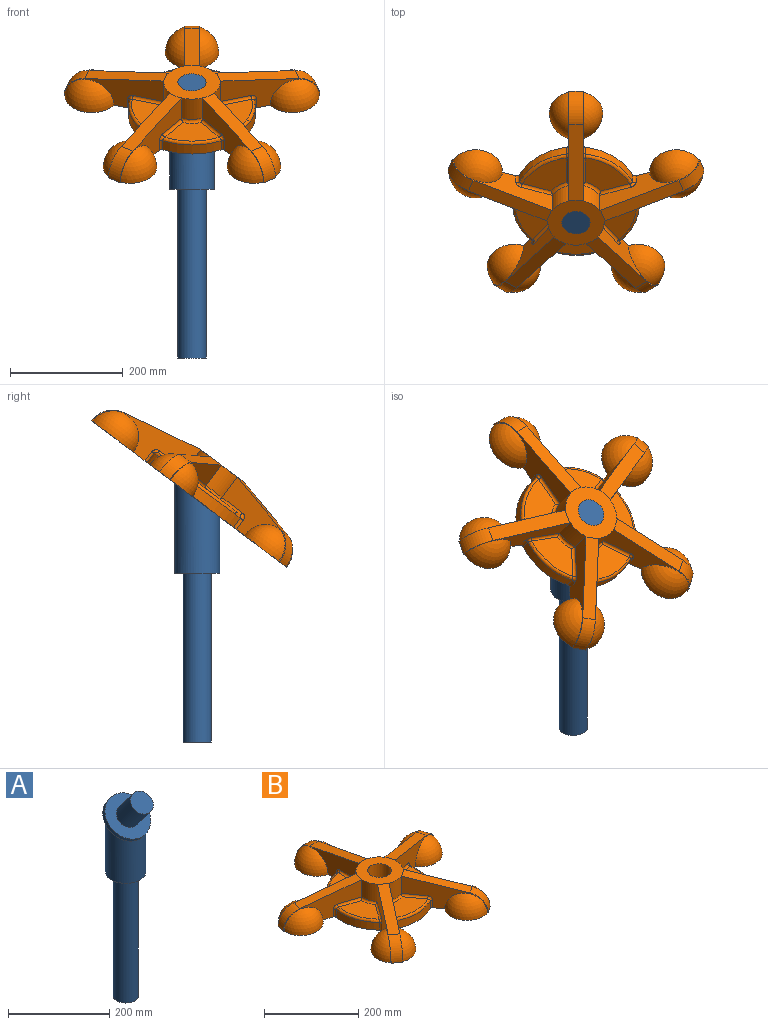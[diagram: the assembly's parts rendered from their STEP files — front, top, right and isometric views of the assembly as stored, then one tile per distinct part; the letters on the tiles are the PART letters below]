
ASSEMBLY  parts=2 mates=1
PART A: 10 faces, bbox 100x105x505 mm
  f0: cylinder r=25mm len=300mm, axis (0,0,1), area 47123.9mm2, adj f1,f3
  f1: plane 50x50mm, normal (0,0,-1), area 1963.5mm2, adj f0
  f2: cylinder r=40mm len=160mm, axis (0,0,-1), area 32672.6mm2, adj f3,f4,f7
  f3: plane 80x80mm, normal (0,0,-1), area 3063.1mm2, adj f0,f2
  f4: plane 80x60mm, normal (0,0.6,-0.8), area 785.4mm2, adj f2,f5
  f5: cylinder r=50mm len=100mm, axis (0,0.6,-0.8), area 3141.6mm2, adj f4,f6,f7
  f6: plane 100x80mm, normal (0,-0.6,0.8), area 5890.5mm2, adj f5,f8
  f7: plane 80x60mm, normal (0,0.6,-0.8), area 785.4mm2, adj f2,f5
  f8: cylinder r=25mm len=82mm, axis (0,0.6,-0.8), area 10210.2mm2, adj f6,f9
  f9: plane 50x40mm, normal (0,-0.6,0.8), area 1963.5mm2, adj f8
PART B: 95 faces, bbox 454.7x434.2x75 mm
  f0: plane 186.59x75mm, normal (1,0,0), area 5066mm2, adj f14,f17,f18,f19,f20,f22,f90,f91
  f1: plane 186.59x75mm, normal (-1,0,0), area 5066mm2, adj f13,f14,f15,f18,f19,f20,f65,f67
  f2: plane 150.95x109.67mm, normal (-0.81,-0.59,0), area 5066mm2, adj f11,f14,f20,f24,f25,f27,f58,f59
  f3: plane 150.95x109.67mm, normal (0.81,0.59,0), area 5066mm2, adj f10,f14,f20,f25,f26,f27,f81,f83
  f4: plane 150.95x109.67mm, normal (-0.81,0.59,0), area 5066mm2, adj f12,f14,f20,f28,f29,f32,f74,f75
  f5: plane 150.95x109.67mm, normal (0.81,-0.59,0), area 5066mm2, adj f11,f14,f20,f29,f30,f32,f53,f54
  f6: plane 177.46x75mm, normal (0.31,0.95,0), area 5066mm2, adj f13,f14,f20,f33,f34,f37,f61,f62
  f7: plane 177.46x75mm, normal (-0.31,-0.95,0), area 5066mm2, adj f12,f14,f20,f34,f35,f37,f69,f70
  f8: plane 177.46x75mm, normal (0.31,-0.95,0), area 5066mm2, adj f10,f14,f20,f40,f41,f42,f77,f78
  f9: plane 177.46x75mm, normal (-0.31,0.95,0), area 5066mm2, adj f14,f20,f22,f38,f41,f42,f85,f86
  f10: cylinder r=50mm len=45mm, axis (0,0,-1), area 1690.4mm2, adj f3,f8,f20,f79
  f11: cylinder r=50mm len=45mm, axis (0,0,-1), area 1690.4mm2, adj f2,f5,f20,f56
  f12: cylinder r=50mm len=45mm, axis (0,0,-1), area 1690.4mm2, adj f4,f7,f20,f72
  f13: cylinder r=50mm len=45mm, axis (0,0,-1), area 1690.4mm2, adj f1,f6,f20,f63
  f14: plane 454.72x434.19mm, normal (0,0,-1), area 48902.3mm2, adj f0,f1,f2,f3,f4,f5,f6,f7
  f15: sphere r=47.5mm, area 5222.9mm2, adj f1,f14
  f16: sphere r=37.5mm, area 8835.7mm2, adj f14
  f17: sphere r=47.5mm, area 5222.9mm2, adj f0,f14
  f18: cylinder r=47.5mm len=46.63mm, axis (-1,0,0), area 1638.2mm2, adj f0,f1,f14,f19
  f19: plane 146.53x28.37mm, normal (0,0.19,0.98), area 3731.2mm2, adj f0,f1,f18,f20
  f20: plane 102.83x100mm, normal (0,0,1), area 5956.2mm2, adj f0,f1,f2,f3,f4,f5,f6,f7
  f21: cylinder r=25mm len=65mm, axis (0,0,-1), area 10210.2mm2, adj f20,f94
  f22: cylinder r=50mm len=45mm, axis (0,0,-1), area 1690.4mm2, adj f0,f9,f20,f88
  f23: sphere r=37.5mm, area 8835.7mm2, adj f14
  f24: sphere r=47.5mm, area 5222.9mm2, adj f2,f14
  f25: cylinder r=47.5mm len=46.63mm, axis (0.81,0.59,0), area 1638.2mm2, adj f2,f3,f14,f27
  f26: sphere r=47.5mm, area 5222.9mm2, adj f3,f14
  f27: plane 133.24x106.35mm, normal (0.11,-0.15,0.98), area 3731.2mm2, adj f2,f3,f20,f25
  f28: sphere r=47.5mm, area 5222.9mm2, adj f4,f14
  f29: cylinder r=47.5mm len=46.63mm, axis (0.81,-0.59,0), area 1638.2mm2, adj f4,f5,f14,f32
  f30: sphere r=47.5mm, area 5222.9mm2, adj f5,f14
  f31: sphere r=37.5mm, area 8835.7mm2, adj f14
  f32: plane 133.24x106.35mm, normal (-0.11,-0.15,0.98), area 3731.2mm2, adj f4,f5,f20,f29
  f33: sphere r=47.5mm, area 5222.9mm2, adj f6,f14
  f34: cylinder r=47.5mm len=46.63mm, axis (-0.31,-0.95,0), area 1638.2mm2, adj f6,f7,f14,f37
  f35: sphere r=47.5mm, area 5222.9mm2, adj f7,f14
  f36: sphere r=37.5mm, area 8835.7mm2, adj f14
  f37: plane 147.08x69.06mm, normal (-0.18,0.06,0.98), area 3731.2mm2, adj f6,f7,f20,f34
  f38: sphere r=47.5mm, area 5222.9mm2, adj f9,f14
  f39: sphere r=37.5mm, area 8835.7mm2, adj f14
  f40: sphere r=47.5mm, area 5222.9mm2, adj f8,f14
  f41: cylinder r=47.5mm len=46.63mm, axis (-0.31,0.95,0), area 1638.2mm2, adj f8,f9,f14,f42
  f42: plane 147.08x69.06mm, normal (0.18,0.06,0.98), area 3731.2mm2, adj f8,f9,f20,f41
  f43: plane 77.97x73.31mm, normal (0,0,1), area 3506.5mm2, adj f86,f88,f89,f90
  f44: cylinder r=112.5mm len=83.87mm, axis (0,0,-1), area 2154.7mm2, adj f14,f85,f89,f92
  f45: plane 91.66x62.69mm, normal (0,0,1), area 3506.5mm2, adj f77,f79,f81,f82
  f46: cylinder r=112.5mm len=98.59mm, axis (0,0,-1), area 2154.7mm2, adj f14,f78,f82,f84
  f47: plane 91.66x62.69mm, normal (0,0,1), area 3506.5mm2, adj f70,f72,f73,f74
  f48: cylinder r=112.5mm len=98.59mm, axis (0,0,-1), area 2154.7mm2, adj f14,f69,f73,f76
  f49: plane 77.97x73.31mm, normal (0,0,1), area 3506.5mm2, adj f61,f63,f65,f66
  f50: cylinder r=112.5mm len=83.87mm, axis (0,0,-1), area 2154.7mm2, adj f14,f62,f66,f68
  f51: cylinder r=112.5mm len=103.67mm, axis (0,0,-1), area 2154.7mm2, adj f14,f53,f57,f60
  f52: plane 96.37x55.03mm, normal (0,0,1), area 3506.5mm2, adj f54,f56,f57,f58
  f53: cylinder r=5mm len=20mm, axis (0,0,-1), area 142.1mm2, adj f5,f14,f51,f55
  f54: cylinder r=5mm len=49.58mm, axis (0.59,0.81,0), area 442mm2, adj f5,f52,f55,f56
  f55: bspline ~12.22x10.6mm, area 81mm2, adj f5,f53,f54,f57
  f56: torus R=55mm, axis (0,0,1), area 283.5mm2, adj f11,f52,f54,f58
  f57: torus R=107.5mm, axis (0,0,1), area 824mm2, adj f51,f52,f55,f59
  f58: cylinder r=5mm len=49.58mm, axis (0.59,-0.81,0), area 442mm2, adj f2,f52,f56,f59
  f59: bspline ~11.81x10.85mm, area 81mm2, adj f2,f57,f58,f60
  f60: cylinder r=5mm len=20mm, axis (0,0,-1), area 142.1mm2, adj f2,f14,f51,f59
  f61: cylinder r=5mm len=56.38mm, axis (-0.95,0.31,0), area 442mm2, adj f6,f49,f63,f64
  f62: cylinder r=5mm len=20mm, axis (0,0,-1), area 142.1mm2, adj f6,f14,f50,f64
  f63: torus R=55mm, axis (0,0,1), area 283.5mm2, adj f13,f49,f61,f65
  f64: bspline ~12.36x11.81mm, area 81mm2, adj f6,f61,f62,f66
  f65: cylinder r=5mm len=57.65mm, axis (0,-1,0), area 442mm2, adj f1,f49,f63,f67
  f66: torus R=107.5mm, axis (0,0,1), area 824mm2, adj f49,f50,f64,f67
  f67: bspline ~12.22x11.78mm, area 81mm2, adj f1,f65,f66,f68
  f68: cylinder r=5mm len=20mm, axis (0,0,-1), area 142.1mm2, adj f1,f14,f50,f67
  f69: cylinder r=5mm len=20mm, axis (0,0,-1), area 142.1mm2, adj f7,f14,f48,f71
  f70: cylinder r=5mm len=56.38mm, axis (0.95,-0.31,0), area 442mm2, adj f7,f47,f71,f72
  f71: bspline ~12.22x11.2mm, area 81mm2, adj f7,f69,f70,f73
  f72: torus R=55mm, axis (0,0,1), area 283.5mm2, adj f12,f47,f70,f74
  f73: torus R=107.5mm, axis (0,0,1), area 824mm2, adj f47,f48,f71,f75
  f74: cylinder r=5mm len=49.58mm, axis (-0.59,-0.81,0), area 442mm2, adj f4,f47,f72,f75
  f75: bspline ~11.81x11.41mm, area 81mm2, adj f4,f73,f74,f76
  f76: cylinder r=5mm len=20mm, axis (0,0,-1), area 142.1mm2, adj f4,f14,f48,f75
  f77: cylinder r=5mm len=56.38mm, axis (0.95,0.31,0), area 442mm2, adj f8,f45,f79,f80
  f78: cylinder r=5mm len=20mm, axis (0,0,-1), area 142.1mm2, adj f8,f14,f46,f80
  f79: torus R=55mm, axis (0,0,1), area 283.5mm2, adj f10,f45,f77,f81
  f80: bspline ~11.83x11.81mm, area 81mm2, adj f8,f77,f78,f82
  f81: cylinder r=5mm len=49.58mm, axis (-0.59,0.81,0), area 442mm2, adj f3,f45,f79,f83
  f82: torus R=107.5mm, axis (0,0,1), area 824mm2, adj f45,f46,f80,f83
  f83: bspline ~12.22x11.89mm, area 81mm2, adj f3,f81,f82,f84
  f84: cylinder r=5mm len=20mm, axis (0,0,-1), area 142.1mm2, adj f3,f14,f46,f83
  f85: cylinder r=5mm len=20mm, axis (0,0,-1), area 142.1mm2, adj f9,f14,f44,f87
  f86: cylinder r=5mm len=56.38mm, axis (-0.95,-0.31,0), area 442mm2, adj f9,f43,f87,f88
  f87: bspline ~12.22x12.02mm, area 81mm2, adj f9,f85,f86,f89
  f88: torus R=55mm, axis (0,0,1), area 283.5mm2, adj f22,f43,f86,f90
  f89: torus R=107.5mm, axis (0,0,1), area 824mm2, adj f43,f44,f87,f91
  f90: cylinder r=5mm len=57.65mm, axis (0,1,0), area 442mm2, adj f0,f43,f88,f91
  f91: bspline ~12.43x11.81mm, area 81mm2, adj f0,f89,f90,f92
  f92: cylinder r=5mm len=20mm, axis (0,0,-1), area 142.1mm2, adj f0,f14,f44,f91
  f93: cylinder r=50mm len=100mm, axis (0,0,-1), area 3141.6mm2, adj f14,f94
  f94: plane 100x100mm, normal (0,0,-1), area 5890.5mm2, adj f21,f93
PLACE A at identity fixed
PLACE B rot(axis=(1,0,0),36.9deg) t=(0,0,130)mm
MATE revolute B.f10 <-> A.f8  axis (0,0.6,-0.8) through (0,-6,138)mm
